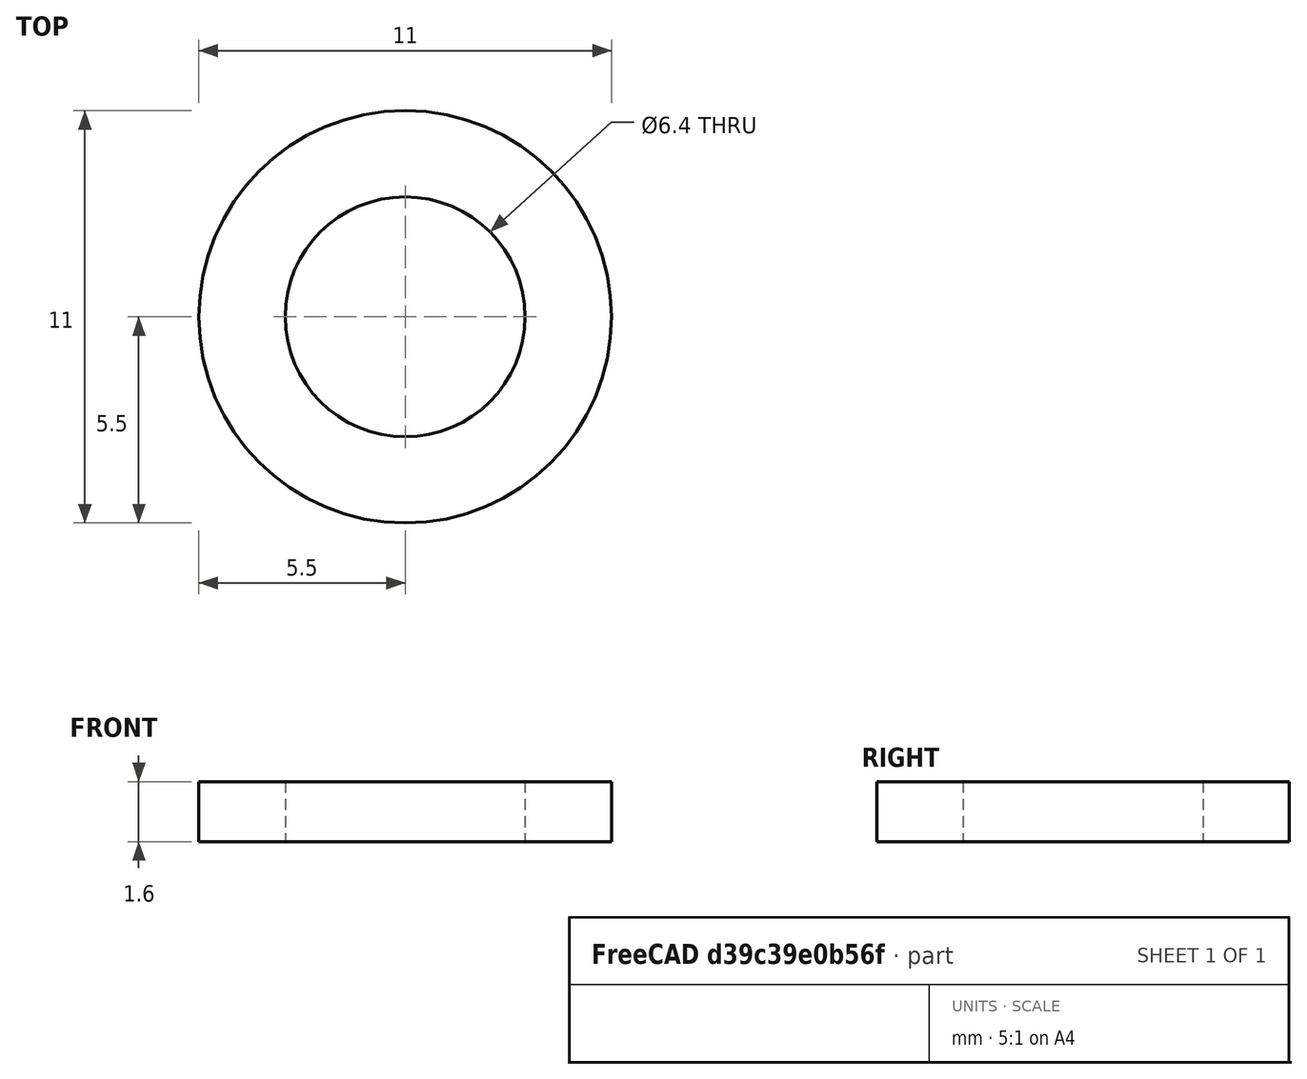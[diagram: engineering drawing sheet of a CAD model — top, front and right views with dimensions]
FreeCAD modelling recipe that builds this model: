
FCSTD DOCUMENT  (FreeCAD 0.14R3700 (Git))
Label: Scheibe DIN 433 - A 6,4
License: CC-BY 3.0
LicenseURL: http://creativecommons.org/licenses/by/3.0/
objects: Sketcher::SketchObject×1, PartDesign::Revolution×1, Part::Feature×1
note: 4 computed .brp shape members not serialized (recipe doc carries the construction recipe); baked Part::Feature solids carry a one-line shape summary decoded from their .brp

FEATURE [Sketcher::SketchObject] Sketch
  Placement = pos=(0,0,0) rot=(0.57735,0.57735,0.57735;2.0944rad)
  sketch-geometry (4):
    g0: LineSegment StartX=3.2 StartY=0 StartZ=0 EndX=5.5 EndY=0 EndZ=0
    g1: LineSegment StartX=5.5 StartY=0 StartZ=0 EndX=5.5 EndY=1.6 EndZ=0
    g2: LineSegment StartX=5.5 StartY=1.6 StartZ=0 EndX=3.2 EndY=1.6 EndZ=0
    g3: LineSegment StartX=3.2 StartY=1.6 StartZ=0 EndX=3.2 EndY=0 EndZ=0
  constraints (12):
    c: Coincident(g0,g1)
    c: Coincident(g1,g2)
    c: Coincident(g2,g3)
    c: Coincident(g3,g0)
    c: Horizontal(g0)
    c: Horizontal(g2)
    c: Vertical(g1)
    c: Vertical(g3)
    c: PointOnObject(g0,g-1)
    c: DistanceY(g1) = 1.6
    c: DistanceX(g-1,g2) = 3.2
    c: DistanceX(g-1,g1) = 5.5
FEATURE [PartDesign::Revolution] Revolution  label="Scheibe DIN 433 - A 6,4 #"
  Angle = 360
  Axis = (0,0,1)
  Base = (0,0,0)
  Placement = pos=(0,0,0) rot=(0.57735,0.57735,0.57735;2.0944rad)
  ReferenceAxis = -> Sketch [V_Axis]
  Reversed = true
  Sketch = -> Sketch
FEATURE [Part::Feature] Revolution001  label="Scheibe DIN 433 - A 6,4 #001"
  Placement = pos=(0,0,0) rot=(0.57735,0.57735,0.57735;2.0944rad)
  shape: bbox 11 x 11 x 1.6 mm, 4 faces (baked)
